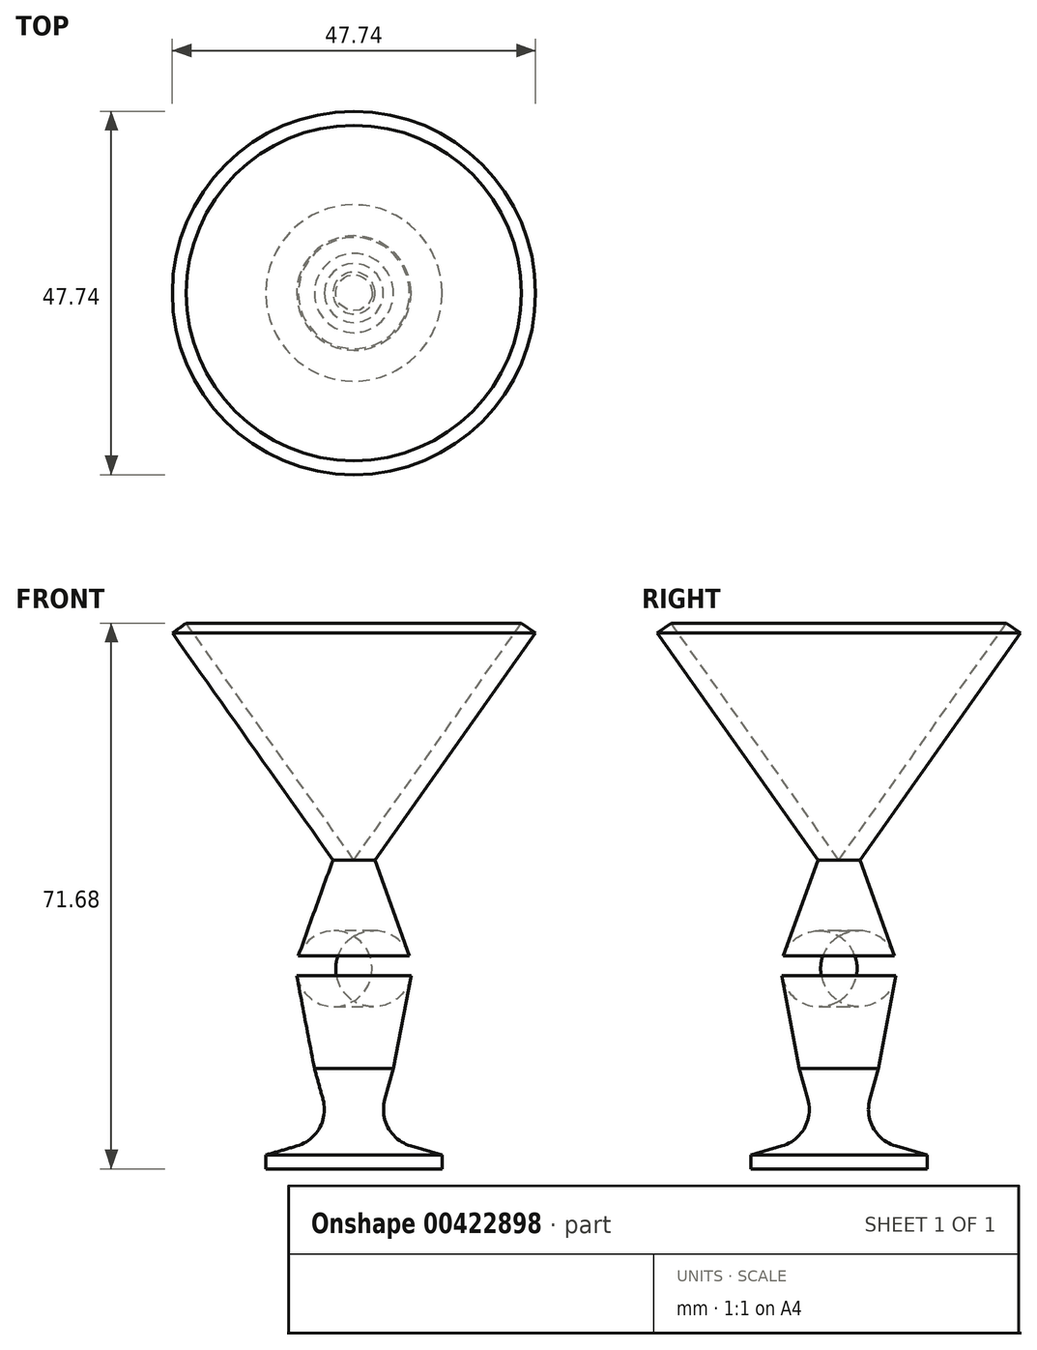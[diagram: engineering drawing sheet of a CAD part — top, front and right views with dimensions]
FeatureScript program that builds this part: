
annotation { "Feature Type Name" : "Feature", "Feature Type Description" : "" }
export const myFeature = defineFeature(function(context is Context, id is Id, definition is map)
    precondition{}
    {
        {
            var Q0;
            Q0=qCreatedBy(makeId("Front.planeOp"),FACE);
            var sketch = newSketch(context, id + "F0", { "sketchPlane" : qUnion([Q0])});
            skLineSegment(sketch, "E0", {"start": v(0, 0) * mm, "end": v(0, 40.57) * mm});
            skLineSegment(sketch, "E1", {"start": v(0, 40.57) * mm, "end": v(22.03, 71.68) * mm});
            skLineSegment(sketch, "E2", {"start": v(22.03, 71.68) * mm, "end": v(23.87, 70.38) * mm});
            skLineSegment(sketch, "E3", {"start": v(23.87, 70.38) * mm, "end": v(2.76, 40.57) * mm});
            skLineSegment(sketch, "E4", {"start": v(2.76, 40.57) * mm, "end": v(7.3, 28) * mm});
            skLineSegment(sketch, "E5", {"start": v(7.51, 25.36) * mm, "end": v(5.16, 13.01) * mm});
            skLineSegment(sketch, "E6", {"start": v(5.25, 13.4) * mm, "end": v(4.07, 9.13) * mm});
            skLineSegment(sketch, "E7", {"start": v(7.5, 3) * mm, "end": v(11.59, 1.81) * mm});
            skLineSegment(sketch, "E8", {"start": v(11.59, 1.81) * mm, "end": v(11.59, 0) * mm});
            skLineSegment(sketch, "E9", {"start": v(11.59, 0) * mm, "end": v(0, 0) * mm});
            skPoint(sketch, "E10.visualSharp", {"position": v(7.77, 26.7) * mm});
            skArc(sketch, "E10.filletArc", {"start": v(7.51, 25.36) * mm, "mid": v(7.59, 26.69) * mm, "end": v(7.3, 28) * mm});
            skPoint(sketch, "E11.visualSharp", {"position": v(5.2, 13.21) * mm});
            skPoint(sketch, "E12.visualSharp", {"position": v(2.76, 4.37) * mm});
            skArc(sketch, "E12.filletArc", {"start": v(4.07, 9.13) * mm, "mid": v(4.53, 5.36) * mm, "end": v(7.5, 3) * mm});
            skSolve(sketch);
        }
        {
            var Q0;
            Q0 = qSketchRegion(id + "F0", true);
            var Q1;
            Q1=sQuery(id+"F0.wireOp",EDGE,"E0");
            revolve(context, id + "F1", {"entities" : qUnion([Q0]), "axis" : qUnion([Q1]), "revolveType" : RevolveType.FULL});
        }
    });
